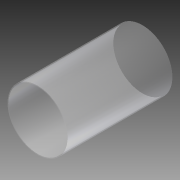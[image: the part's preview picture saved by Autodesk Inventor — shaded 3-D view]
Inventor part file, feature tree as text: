
AUTODESK INVENTOR PART (.ipt)
format: ipt  version: 2015 (Build 190159000, 159)  size: 86,016 bytes
history: native  units: mm
features: extrude x1, sketch x1
ambient origin geometry x8: Origin, YZ Plane, XZ Plane, XY Plane, X Axis, Y Axis, Z Axis, Center Point
bodies: Solid1 (feature_tree)
feature tree (2):
  extrude  "Extrusion1"  Depth=180.0mm
  sketch  "Sketch1"  dims[d0=103.0mm d1=100.0mm d2=180.0mm d3=0.0mm]
